# Revit family: Gira_014003
name_source: partatom
category: Electrical Fixtures
revit_build: Autodesk Revit 2017 (Build: 20160225_1515(x64)
units: mm (PartAtom-declared; Revit-internal decimal feet)

## family parameters
Cut with Voids When Loaded = No
Host = Face
Maintain Annotation Orientation = Yes
Part Type = Normal
Room Calculation Point = No
Round Connector Dimension = Use Diameter
Shared = No

## types (1)
- Hotel-card btn 2-way m-c (ill.) in.sp. System 55 p.white
    Assembly arrangement = Basic element with central cover plate
    Available = No
    BIM (1) = https://media.stage.bim.site und Tasten.rfa?public/gira/36a6b08/Sys55_Komplettgerät_Schalten und Tasten.rfa
    Category = Push-switch button
    Colour = White
    Data sheet (1) = https://katalog.gira.de
    Default Elevation = 1219 mm
    Description = Hotel-crd 2-w m-c cbi in.sp. Sys55 PW,Hotel-card button 10 AX 250 V~ can be illuminated with inscription space,2-way momentary-contact, 1-pole,pure white glossy,Features:,- Applications of the hotel-card button with disassembly safeguard include performing security and energy-saving functions.,- When the hotel card is removed, any devices which are still switched on are deactivated.,- The electric circuit via the push button is only activated when the card has been inserted.,,Notes :,- Further versions are available upon request.
    GTIN = 4010337140030
    HAN = 014003
    Halogen free = Yes
    HeinzeBIM = https://bimportal.heinze.de
    Imprint = None
    Label space/information surface = Yes
    Manufacturer = Gira
    Manufacturer URL = https://www.gira.de
    Material = Plastic
    Material quality = Thermoplastic
    Method of operation = Hotel card
    Model = Single push button
    Mounting method = Flush mounted (plaster)
    Name = Hotel-card btn 2-way m-c (ill.) in.sp. System 55 p.white
    Nominal voltage = 250
    Number of rockers = 1
    RAL-number (akin) = 9010
    Rated current = 10
    Suitable for degree of protection (IP) = IP20
    Surface finishing = Glossy
    Surface protection = Other
    Transparent = No
    Type of fastening = Mounting with claw and screw
    URL = http://katalog.gira.de
    With lighting = No

## geometry (parser evidence)
native form markers: Sweep x3
no freeform markers — native parametric forms only
